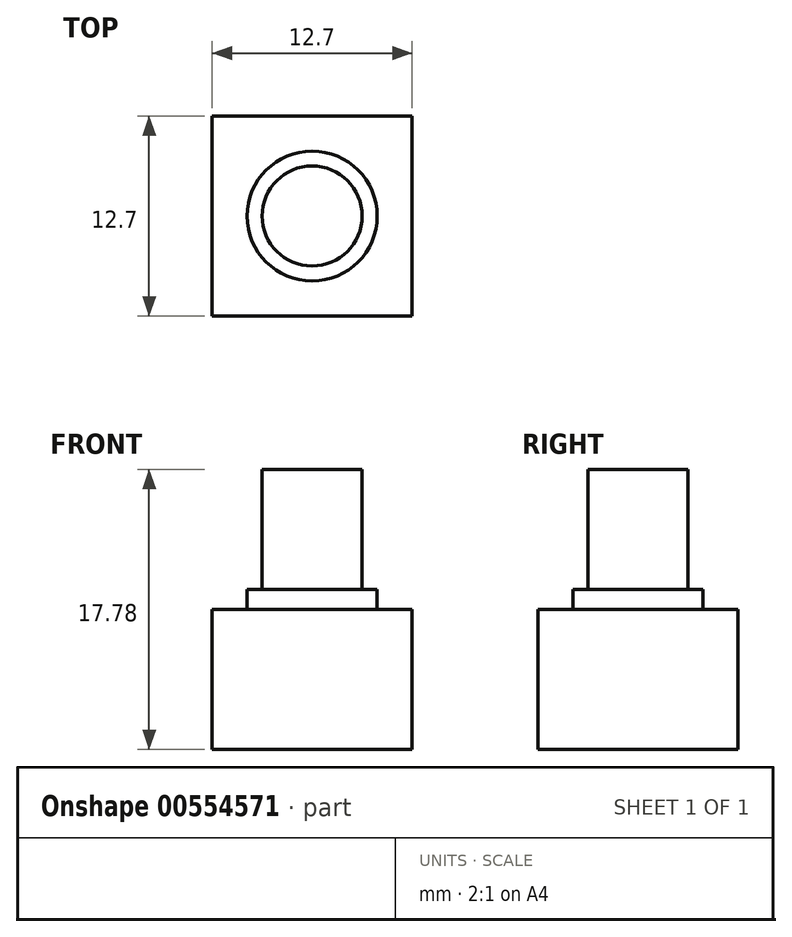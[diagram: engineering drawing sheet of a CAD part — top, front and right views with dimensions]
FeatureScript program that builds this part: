
annotation { "Feature Type Name" : "Feature", "Feature Type Description" : "" }
export const myFeature = defineFeature(function(context is Context, id is Id, definition is map)
    precondition{}
    {
        {
            var Q0;
            Q0=qCreatedBy(makeId("Top.planeOp"),FACE);
            var sketch = newSketch(context, id + "F0", { "sketchPlane" : qUnion([Q0])});
            skLineSegment(sketch, "E0.bottom", {"start": v(6.35, 6.35) * mm, "end": v(-6.35, 6.35) * mm});
            skLineSegment(sketch, "E0.top", {"start": v(6.35, -6.35) * mm, "end": v(-6.35, -6.35) * mm});
            skLineSegment(sketch, "E0.left", {"start": v(6.35, 6.35) * mm, "end": v(6.35, -6.35) * mm});
            skLineSegment(sketch, "E0.right", {"start": v(-6.35, 6.35) * mm, "end": v(-6.35, -6.35) * mm});
            skPoint(sketch, "E0.middle", {"position": v(0, 0) * mm});
            skSolve(sketch);
        }
        {
            var Q0;
            Q0 = qSketchRegion(id + "F0", true);
            extrude(context, id + "F1", {"entities" : qUnion([Q0]), "depth" : 8.9 * mm, "offsetDistance" : 25.4 * mm});
        }
        {
            var Q0;
            Q0=makeQuery(id+"F1.opExtrude","CAP_FACE",FACE,{"disambiguationData":[OSD([sQuery(id+"F0.wireOp",EDGE,"E0.bottom"),sQuery(id+"F0.wireOp",EDGE,"E0.top"),sQuery(id+"F0.wireOp",EDGE,"E0.left"),sQuery(id+"F0.wireOp",EDGE,"E0.right")])],"isStart":false});
            var sketch = newSketch(context, id + "F2", { "sketchPlane" : qUnion([Q0])});
            skCircle(sketch, "E1", {"center": v(0, 0) * mm, "radius": 4.13 * mm});
            skSolve(sketch);
        }
        {
            var Q0;
            Q0 = qSketchRegion(id + "F2", true);
            extrude(context, id + "F3", {"entities" : qUnion([Q0]), "operationType" : NewBodyOperationType.ADD, "depth" : 1.27 * mm, "offsetDistance" : 25.4 * mm});
        }
        {
            var Q0;
            Q0=makeQuery(id+"F3.opExtrude","CAP_FACE",FACE,{"disambiguationData":[OSD([sQuery(id+"F2.wireOp",EDGE,"E1")])],"isStart":false});
            var sketch = newSketch(context, id + "F4", { "sketchPlane" : qUnion([Q0])});
            skCircle(sketch, "E2", {"center": v(0, 0) * mm, "radius": 3.18 * mm});
            skSolve(sketch);
        }
        {
            var Q0;
            Q0 = qSketchRegion(id + "F4", true);
            extrude(context, id + "F5", {"entities" : qUnion([Q0]), "operationType" : NewBodyOperationType.ADD, "depth" : 7.62 * mm, "offsetDistance" : 25.4 * mm});
        }
        {
            var Q0;
            Q0=qCreatedBy(makeId("Right.planeOp"),FACE);
            var sketch = newSketch(context, id + "F6", { "sketchPlane" : qUnion([Q0])});
            skLineSegment(sketch, "E3", {"start": v(0, 15.24) * mm, "end": v(-4.34, 27.17) * mm, "construction": true});
            skSolve(sketch);
        }
    });
